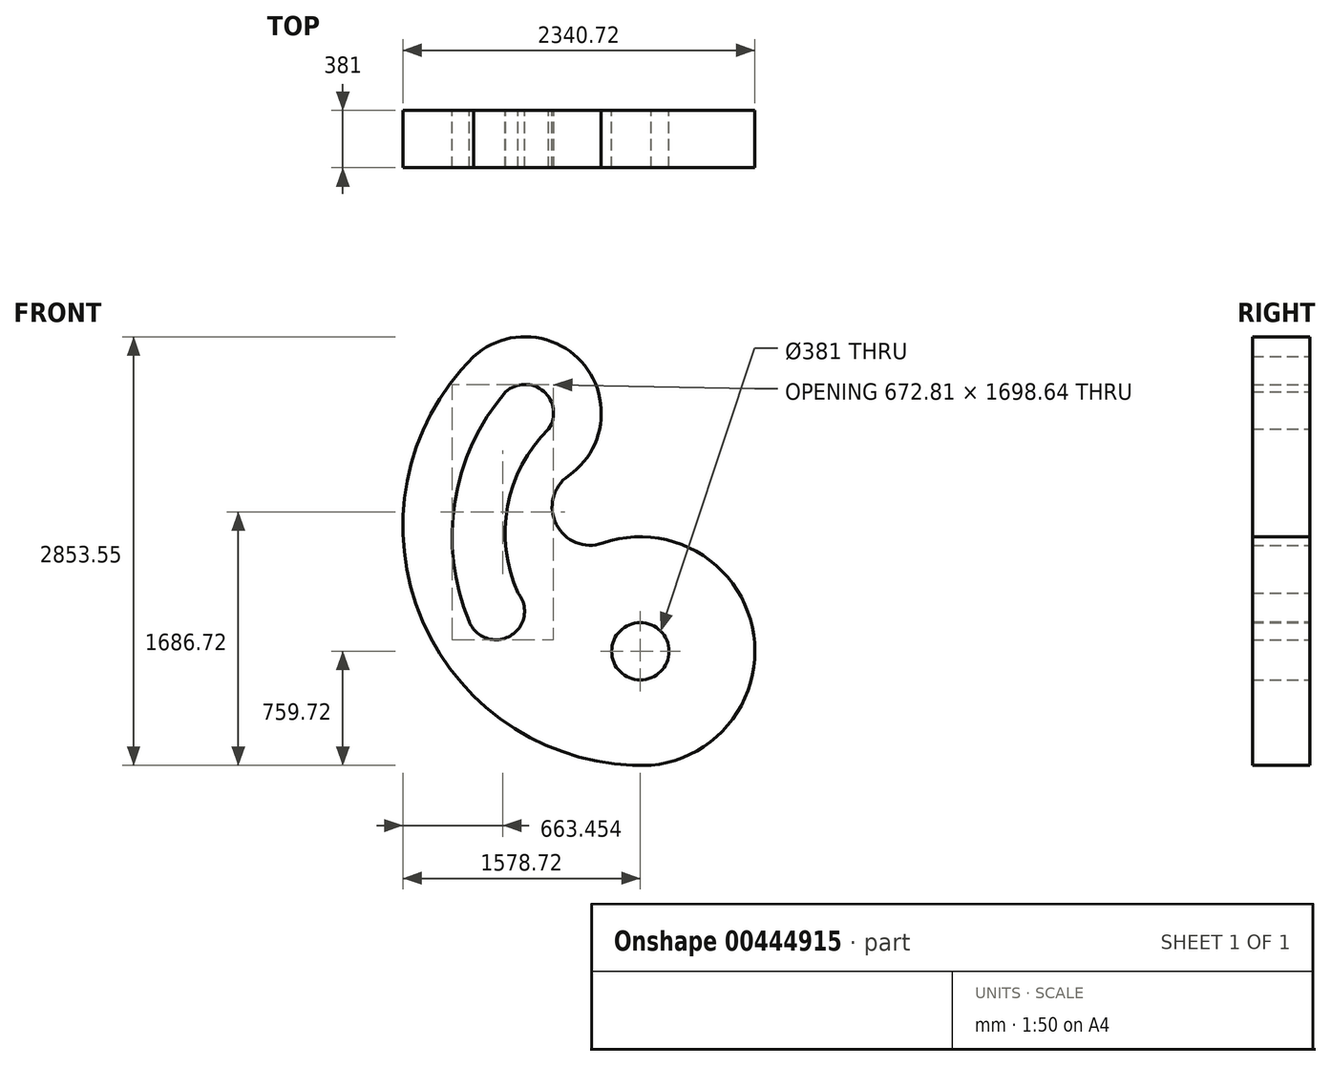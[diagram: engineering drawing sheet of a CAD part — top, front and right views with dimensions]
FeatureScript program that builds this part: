
annotation { "Feature Type Name" : "Feature", "Feature Type Description" : "" }
export const myFeature = defineFeature(function(context is Context, id is Id, definition is map)
    precondition{}
    {
        {
            var Q0;
            Q0=qCreatedBy(makeId("Front.planeOp"),FACE);
            var sketch = newSketch(context, id + "F0", { "sketchPlane" : qUnion([Q0])});
            skArc(sketch, "E0", {"start": v(28.32, -761.47) * mm, "mid": v(748.91, 140.6) * mm, "end": v(-249.8, 719.9) * mm});
            skCircle(sketch, "E1", {"center": v(0, 0) * mm, "radius": 190.5 * mm});
            skArc(sketch, "E2", {"start": v(-477.9, 1168.51) * mm, "mid": v(-559.49, 844.73) * mm, "end": v(-249.8, 719.9) * mm});
            skArc(sketch, "E3", {"start": v(-477.9, 1168.51) * mm, "mid": v(-369.42, 1901.33) * mm, "end": v(-1107.63, 1963.23) * mm});
            skArc(sketch, "E4", {"start": v(-608.96, 1480.32) * mm, "mid": v(-643.44, 1730.34) * mm, "end": v(-895.8, 1726.73) * mm});
            skArc(sketch, "E5", {"start": v(28.32, -761.47) * mm, "mid": v(49.7, -760.22) * mm, "end": v(71.08, -758.68) * mm});
            skArc(sketch, "E6", {"start": v(-1107.63, 1963.23) * mm, "mid": v(-1447.6, 199.84) * mm, "end": v(71.08, -758.68) * mm});
            skArc(sketch, "E7", {"start": v(-1138.42, 198.58) * mm, "mid": v(-865.28, 102.5) * mm, "end": v(-812.73, 387.25) * mm});
            skArc(sketch, "E8", {"start": v(-895.8, 1726.73) * mm, "mid": v(-1234.58, 991.5) * mm, "end": v(-1134.06, 188.23) * mm});
            skArc(sketch, "E9", {"start": v(-608.96, 1480.32) * mm, "mid": v(-888.93, 925.6) * mm, "end": v(-776.2, 314.53) * mm});
            skSolve(sketch);
        }
        {
            var Q0;
            Q0=makeQuery(id+"F0.imprint","IMPRINT",FACE,{"disambiguationData":[TD([[makeQuery(id+"F0.imprint","IMPRINT",EDGE,{"derivedFrom":sQuery(id+"F0.wireOp",EDGE,"E1")}),-1.0]])]});
            extrude(context, id + "F1", {"entities" : qUnion([Q0]), "depth" : 381 * mm});
        }
    });
